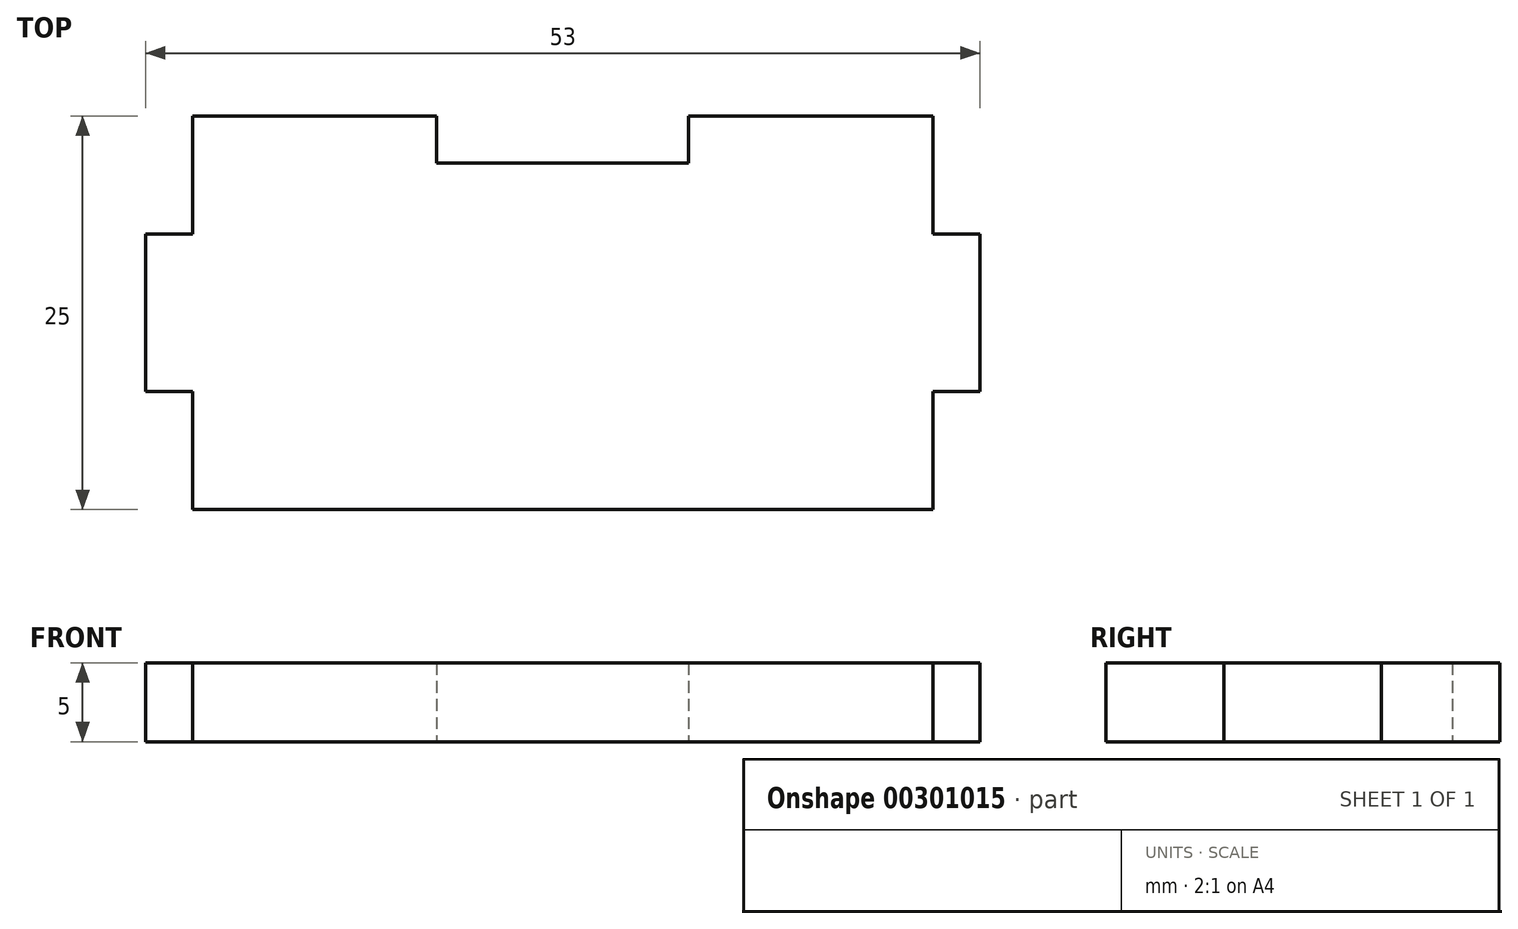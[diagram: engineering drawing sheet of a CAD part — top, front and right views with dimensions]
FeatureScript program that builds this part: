
annotation { "Feature Type Name" : "Feature", "Feature Type Description" : "" }
export const myFeature = defineFeature(function(context is Context, id is Id, definition is map)
    precondition{}
    {
        {
            var Q0;
            Q0=qCreatedBy(makeId("Top.planeOp"),FACE);
            var sketch = newSketch(context, id + "F0", { "sketchPlane" : qUnion([Q0])});
            skLineSegment(sketch, "E0", {"start": v(23.5, 12.5) * mm, "end": v(23.5, 5) * mm});
            skLineSegment(sketch, "E1", {"start": v(23.5, -12.5) * mm, "end": v(23.5, -5) * mm});
            skLineSegment(sketch, "E2", {"start": v(23.5, 5) * mm, "end": v(26.5, 5) * mm});
            skLineSegment(sketch, "E3", {"start": v(23.5, -5) * mm, "end": v(26.5, -5) * mm});
            skLineSegment(sketch, "E4", {"start": v(26.5, 5) * mm, "end": v(26.5, -5) * mm});
            skLineSegment(sketch, "E5.MirrorCS", {"start": v(-26.5, 5) * mm, "end": v(-26.5, -5) * mm});
            skLineSegment(sketch, "E6.MirrorCS", {"start": v(-23.5, 5) * mm, "end": v(-26.5, 5) * mm});
            skLineSegment(sketch, "E7.MirrorCS", {"start": v(-23.5, -5) * mm, "end": v(-26.5, -5) * mm});
            skLineSegment(sketch, "E8.MirrorCS", {"start": v(-23.5, -12.5) * mm, "end": v(-23.5, -5) * mm});
            skLineSegment(sketch, "E9.MirrorCS", {"start": v(-23.5, 12.5) * mm, "end": v(-23.5, 5) * mm});
            skLineSegment(sketch, "E10", {"start": v(-23.5, 12.5) * mm, "end": v(-8, 12.5) * mm});
            skLineSegment(sketch, "E11", {"start": v(23.5, 12.5) * mm, "end": v(8, 12.5) * mm});
            skLineSegment(sketch, "E12", {"start": v(-8, 12.5) * mm, "end": v(-8, 9.5) * mm});
            skLineSegment(sketch, "E13", {"start": v(8, 12.5) * mm, "end": v(8, 9.5) * mm});
            skLineSegment(sketch, "E14", {"start": v(-8, 9.5) * mm, "end": v(8, 9.5) * mm});
            skLineSegment(sketch, "E15", {"start": v(-23.5, -12.5) * mm, "end": v(23.5, -12.5) * mm});
            skSolve(sketch);
        }
        {
            var Q0;
            Q0=makeQuery(id+"F0.imprint","IMPRINT",FACE,{"disambiguationData":[TD([[makeQuery(id+"F0.imprint","IMPRINT",EDGE,{"derivedFrom":sQuery(id+"F0.wireOp",EDGE,"E0")}),-1.0]])]});
            extrude(context, id + "F1", {"entities" : qUnion([Q0]), "depth" : 5 * mm, "offsetDistance" : 25 * mm});
        }
    });
